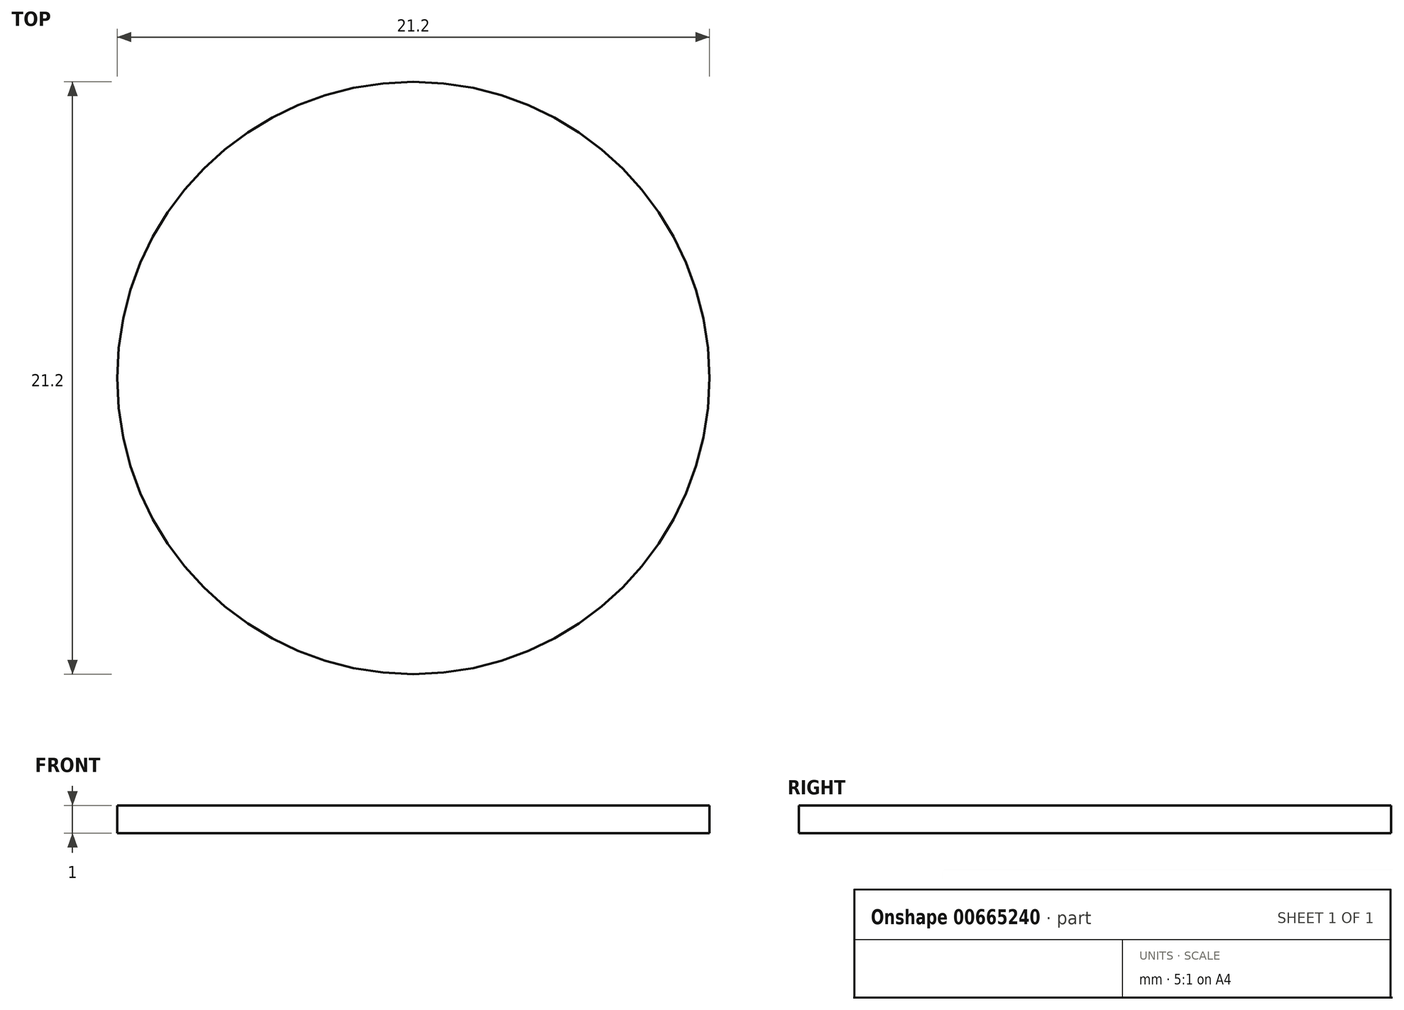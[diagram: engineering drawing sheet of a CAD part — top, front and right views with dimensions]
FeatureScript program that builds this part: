
annotation { "Feature Type Name" : "Feature", "Feature Type Description" : "" }
export const myFeature = defineFeature(function(context is Context, id is Id, definition is map)
    precondition{}
    {
        {
            var Q0;
            Q0=qCreatedBy(makeId("Top.planeOp"),FACE);
            var sketch = newSketch(context, id + "F0", { "sketchPlane" : qUnion([Q0])});
            skCircle(sketch, "E0", {"center": v(0, 0) * mm, "radius": 10.6 * mm});
            skSolve(sketch);
        }
        {
            var Q0;
            Q0 = qSketchRegion(id + "F0", true);
            extrude(context, id + "F1", {"entities" : qUnion([Q0]), "depth" : 1 * mm, "offsetDistance" : 25 * mm});
        }
    });
